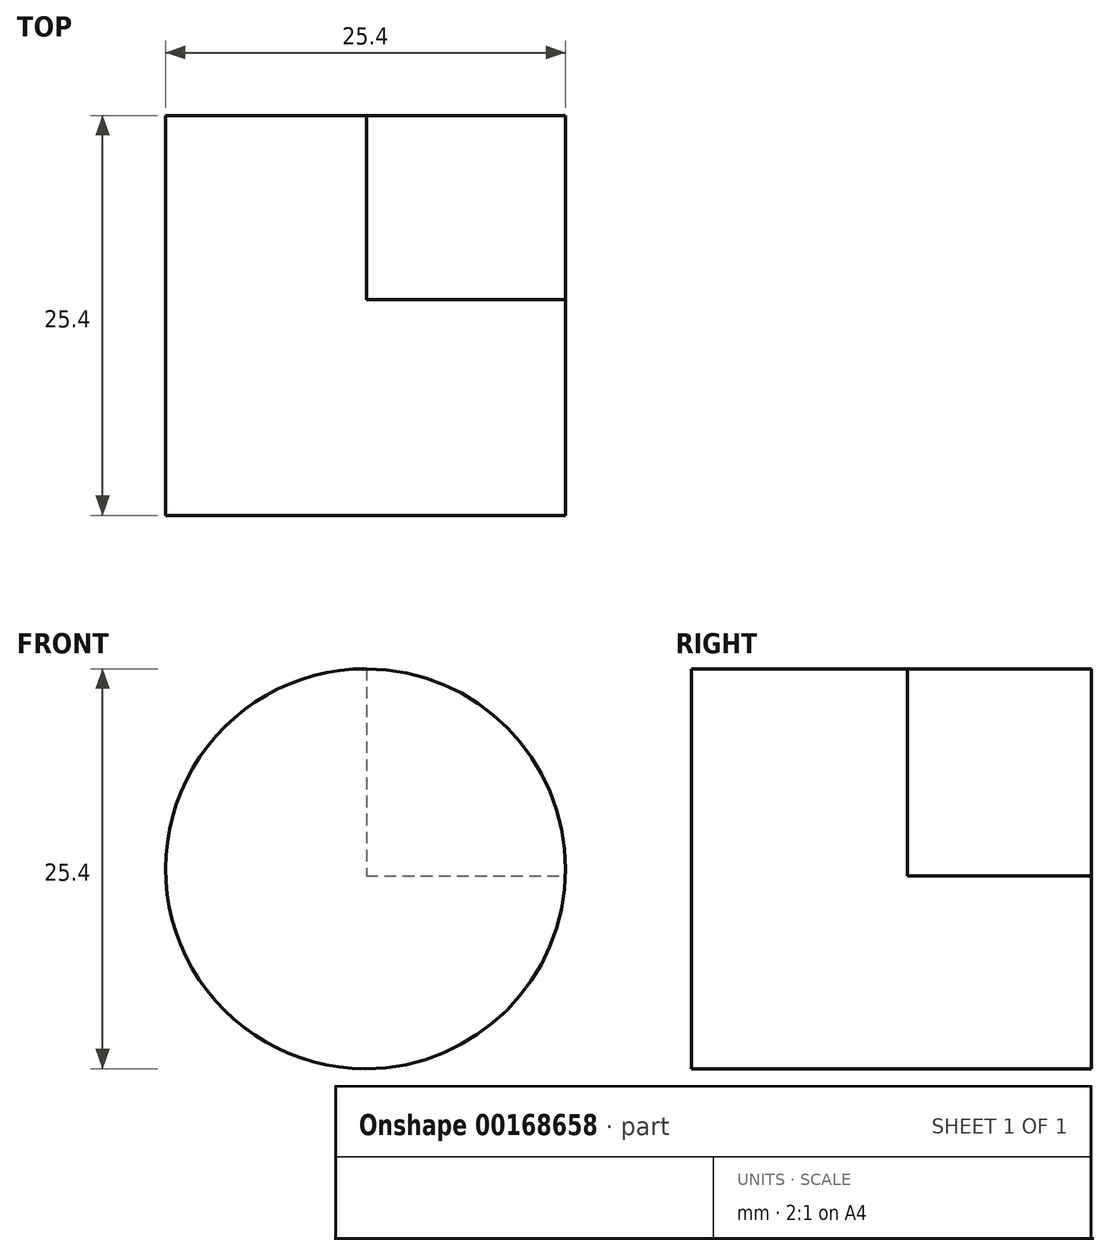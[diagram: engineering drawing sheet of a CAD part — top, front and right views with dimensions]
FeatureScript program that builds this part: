
annotation { "Feature Type Name" : "Feature", "Feature Type Description" : "" }
export const myFeature = defineFeature(function(context is Context, id is Id, definition is map)
    precondition{}
    {
        {
            var Q0;
            Q0=qCreatedBy(makeId("Front.planeOp"),FACE);
            var sketch = newSketch(context, id + "F0", { "sketchPlane" : qUnion([Q0])});
            skLineSegment(sketch, "E0.bottom", {"start": v(-12.95, 27.48) * mm, "end": v(12.45, 27.48) * mm});
            skLineSegment(sketch, "E0.top", {"start": v(-12.95, 2.08) * mm, "end": v(12.45, 2.08) * mm});
            skLineSegment(sketch, "E0.left", {"start": v(-12.95, 27.48) * mm, "end": v(-12.95, 2.08) * mm});
            skLineSegment(sketch, "E0.right", {"start": v(12.45, 27.48) * mm, "end": v(12.45, 2.08) * mm});
            skSolve(sketch);
        }
        {
            var Q0;
            Q0=qCreatedBy(makeId("Front.planeOp"),FACE);
            var sketch = newSketch(context, id + "F1", { "sketchPlane" : qUnion([Q0])});
            skCircle(sketch, "E1", {"center": v(-13, 2.53) * mm, "radius": 12.7 * mm});
            skSolve(sketch);
        }
        {
            var Q0;
            Q0=makeQuery(id+"F1.imprint","IMPRINT",FACE,{"disambiguationData":[TD([[makeQuery(id+"F1.imprint","IMPRINT",EDGE,{"derivedFrom":sQuery(id+"F1.wireOp",EDGE,"E1")}),1.0]])]});
            extrude(context, id + "F2", {"entities" : qUnion([Q0]), "depth" : 25.4 * mm});
        }
        {
            var Q0;
            Q0=makeQuery(id+"F0.imprint","IMPRINT",FACE,{"disambiguationData":[TD([[makeQuery(id+"F0.imprint","IMPRINT",EDGE,{"derivedFrom":sQuery(id+"F0.wireOp",EDGE,"E0.bottom")}),-1.0]])]});
            extrude(context, id + "F3", {"entities" : qUnion([Q0]), "operationType" : NewBodyOperationType.REMOVE, "depth" : 11.68 * mm});
        }
    });
